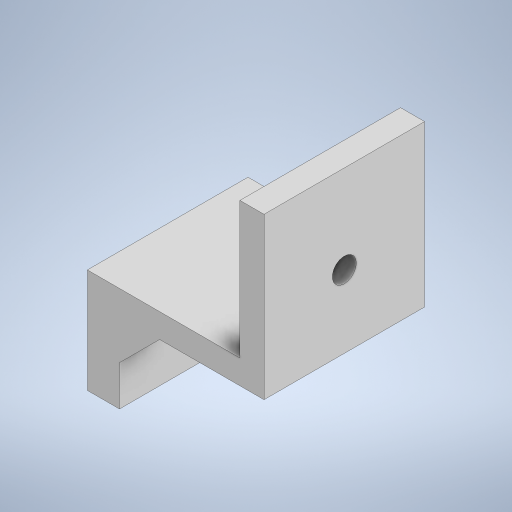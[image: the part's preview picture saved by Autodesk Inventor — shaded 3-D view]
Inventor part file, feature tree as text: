
AUTODESK INVENTOR PART (.ipt)
format: ipt  version: 2023 (Build 270158000, 158)  size: 271,360 bytes
history: native  units: in
note: dims shown in document units (in); Inventor stores cm internally (conversion verified against a paired STEP export)
features: extrude x7, sketch x7
ambient origin geometry x8: Origin, YZ Plane, XZ Plane, XY Plane, X Axis, Y Axis, Z Axis, Center Point
bodies: Solid1 (feature_tree)
feature tree (14):
  extrude  "Extrusion1"  Depth=0.7874in
  extrude  "Extrusion4"  Depth=0.1181in
  extrude  "Extrusion5"  Depth=0.7874in TaperAngle=0.0deg
  extrude  "Extrusion6"  Depth=0.1575in
  extrude  "Extrusion7"  Depth=0.7874in TaperAngle=0.0deg
  extrude  "Extrusion8"  Depth=0.3937in
  extrude  "Extrusion9"  TaperAngle=0.0deg  [1 undecoded]
  sketch  "Sketch1"  dims[d0=0.8661in d1=0.7874in]
  sketch  "Sketch4"  dims[d2=0.1181in d3=0.1181in]
  sketch  "Sketch5"  dims[d4=0.1181in d5=0.7874in d6=0.0in]
  sketch  "Sketch6"  dims[d15=0.0in d16=0.0in d17=0.1575in]
  sketch  "Sketch7"  dims[d18=0.3937in d19=0.7874in d20=0.0in]
  sketch  "Sketch8"  dims[d21=0.1969in d22=0.3937in]
  sketch  "Sketch9"  dims[d23=0.1969in d24=0.0in d25=0.0in d26=0.1969in d27=0.1969in d28=0.1575in d29=0.0in d30=0.1969in d31=0.1969in d32=0.1575in d33=0.0in d34=0.3937in d35=0.2362in d36=0.1181in d37=0.0in d38=0.0in]
note: 1 required parameter value undecoded (feature->parameter linkage not recoverable at this tier; creation-order binding heuristic only, values carry confidence <= 0.55)
